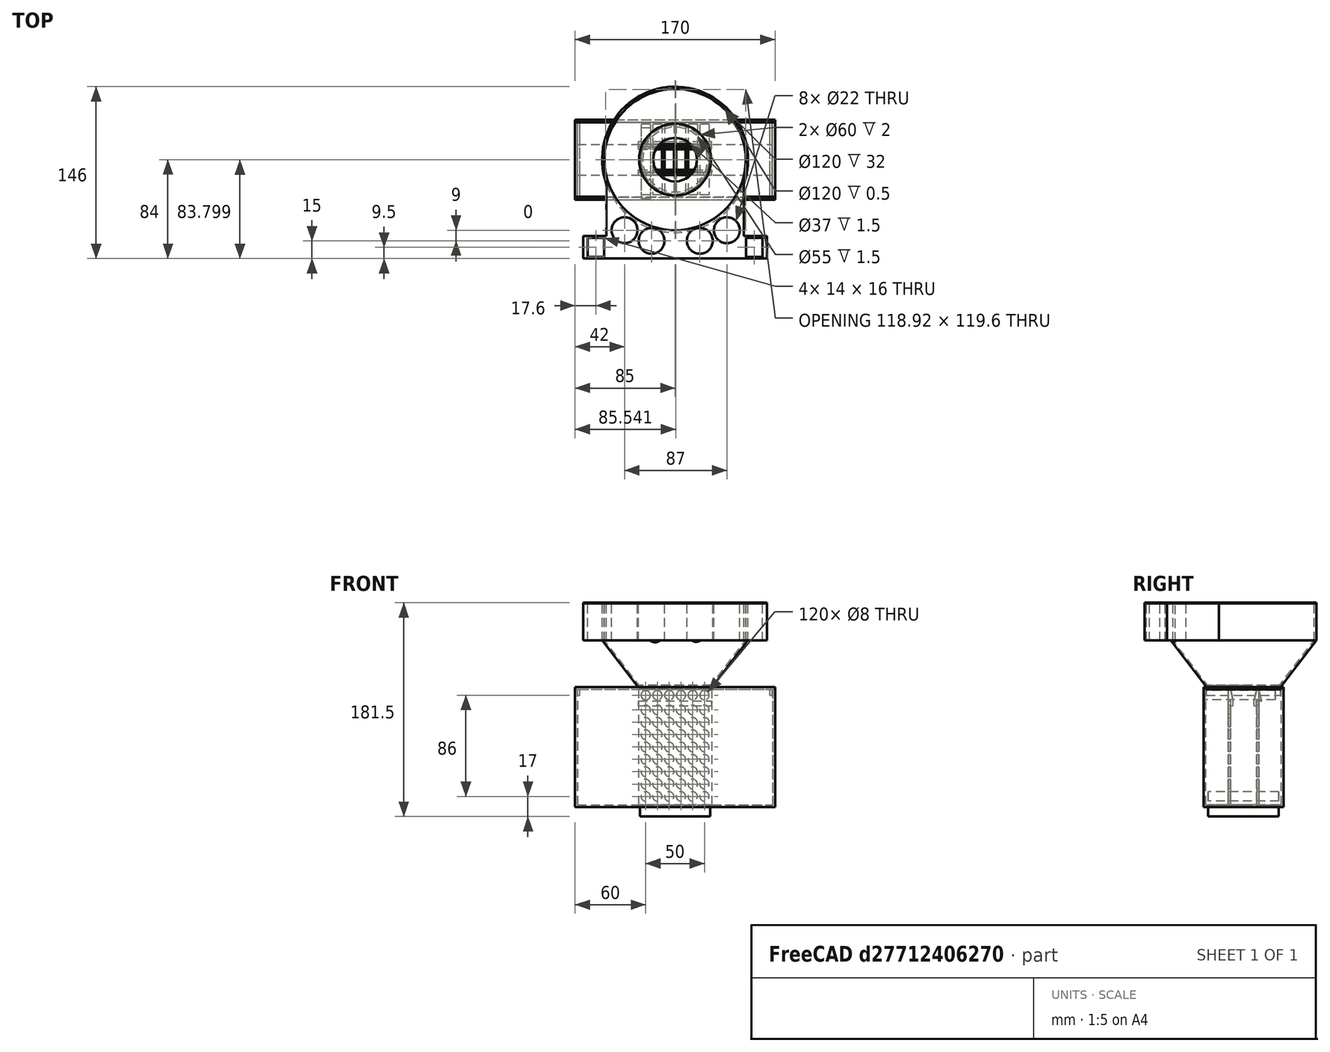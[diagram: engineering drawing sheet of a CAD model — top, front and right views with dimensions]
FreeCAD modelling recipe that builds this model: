
FCSTD DOCUMENT  (FreeCAD 0.19R24291 (Git))
Label: ventilador2
License: All rights reserved
LicenseURL: http://en.wikipedia.org/wiki/All_rights_reserved
objects: Part::Box×38, Part::Cut×37, Part::Cylinder×23, Part::MultiFuse×13, Part::FeaturePython×7, Part::Feature×7, Mesh::Feature×5, Part::Cone×4, Sketcher::SketchObject×1, PartDesign::Pad×1, PartDesign::Body×1
note: 129 computed .brp shape members not serialized (recipe doc carries the construction recipe); baked Part::Feature solids carry a one-line shape summary decoded from their .brp

FEATURE [Part::Box] Box  label="freeze1"
  AttacherType = Attacher::AttachEngine3D
  Height = 98
  Length = 166
  Width = 19
FEATURE [Part::Box] Box001  label="freeze2"
  AttacherType = Attacher::AttachEngine3D
  Height = 98
  Length = 166
  Placement = pos=(0,45,0) rot=(0,0,1;0rad)
  Width = 19
FEATURE [Part::Box] Box002  label="Cube"
  AttacherType = Attacher::AttachEngine3D
  Height = 2
  Length = 170
  Placement = pos=(-2,-2,-2) rot=(0,0,1;0rad)
  Width = 68
FEATURE [Part::Box] Box003  label="Cube001"
  AttacherType = Attacher::AttachEngine3D
  Height = 100
  Length = 170
  Placement = pos=(-2,-2,0) rot=(0,0,1;0rad)
  Width = 2
FEATURE [Part::Box] Box004  label="Cube002"
  AttacherType = Attacher::AttachEngine3D
  Height = 88
  Length = 170
  Placement = pos=(-2,19,0) rot=(0,0,1;0rad)
  Width = 2
FEATURE [Part::Box] Box005  label="Cube003"
  AttacherType = Attacher::AttachEngine3D
  Height = 88
  Length = 170
  Placement = pos=(-2,43,0) rot=(0,0,1;0rad)
  Width = 2
FEATURE [Part::Box] Box006  label="Cube004"
  AttacherType = Attacher::AttachEngine3D
  Height = 100
  Length = 170
  Placement = pos=(-2,64,0) rot=(0,0,1;0rad)
  Width = 2
FEATURE [Part::Box] Box007  label="Cube005"
  AttacherType = Attacher::AttachEngine3D
  Height = 98
  Length = 2
  Placement = pos=(-2,0,0) rot=(0,0,1;0rad)
  Width = 64
FEATURE [Part::Box] Box008  label="Cube006"
  AttacherType = Attacher::AttachEngine3D
  Height = 98
  Length = 2
  Placement = pos=(166,0,0) rot=(0,0,1;0rad)
  Width = 66
FEATURE [Part::MultiFuse] Fusion  label="base_caja"
  Shapes = -> [Box002,Box003,Box004,Box005,Box006,Box007,Box008]
FEATURE [Part::Box] Box009  label="Cube007"
  AttacherType = Attacher::AttachEngine3D
  Height = 12
  Length = 165
  Placement = pos=(0.5,19,88) rot=(0,0,1;0rad)
  Width = 2
FEATURE [Part::Box] Box010  label="Cube008"
  AttacherType = Attacher::AttachEngine3D
  Height = 12
  Length = 165
  Placement = pos=(0.5,43.2,88) rot=(0,0,1;0rad)
  Width = 2
FEATURE [Part::Box] Box011  label="Cube009"
  AttacherType = Attacher::AttachEngine3D
  Height = 2
  Length = 170
  Placement = pos=(-2,0.5,98) rot=(0,0,1;0rad)
  Width = 63
FEATURE [Part::MultiFuse] Fusion001  label="tapa_caja"
  Shapes = -> [Box009,Box010,Box011]
FEATURE [Part::Cylinder] Cylinder
  Angle = 360
  AttacherType = Attacher::AttachEngine3D
  Height = 10
  Placement = pos=(83,32,98) rot=(0,0,1;0rad)
  Radius = 30
FEATURE [Part::FeaturePython] Point  label="Center"  # WARN: FeaturePython — macro-defined, semantics opaque (R4)
  X = 83
  Y = 32
  Z = 108
FEATURE [Part::Cylinder] Cylinder001
  Angle = 360
  AttacherType = Attacher::AttachEngine3D
  Height = 10
  Placement = pos=(83,32,-10) rot=(0,0,1;0rad)
  Radius = 30
FEATURE [Part::Cylinder] Cylinder002
  Angle = 360
  AttacherType = Attacher::AttachEngine3D
  Height = 10
  Placement = pos=(83,32,-10) rot=(0,0,1;0rad)
  Radius = 30
FEATURE [Part::Cut] Cut  label="base1"
  Base = -> Fusion
  Tool = -> Cylinder001
FEATURE [Part::Cut] Cut001  label="tapa1"
  Base = -> Fusion001
  Tool = -> Cylinder
FEATURE [Part::Box] Box012  label="Cube010"
  AttacherType = Attacher::AttachEngine3D
  Height = 10
  Length = 52
  Placement = pos=(0,5,88) rot=(0,0,1;0rad)
  Width = 45
FEATURE [Part::Box] Box013  label="Cube011"
  AttacherType = Attacher::AttachEngine3D
  Height = 10
  Length = 52
  Placement = pos=(114,5,88) rot=(0,0,1;0rad)
  Width = 45
FEATURE [Part::Cut] Cut002
  Base = -> Cut001
  Tool = -> Box012
FEATURE [Part::Cut] Cut003
  Base = -> Cut002
  Tool = -> Box013
FEATURE [Part::Box] Box014  label="Cube012"
  AttacherType = Attacher::AttachEngine3D
  Height = 4
  Length = 48
  Placement = pos=(59,19,96) rot=(0,0,1;0rad)
  Width = 2
FEATURE [Part::Box] Box015  label="Cube013"
  AttacherType = Attacher::AttachEngine3D
  Height = 4
  Length = 48
  Placement = pos=(59,43.2,96) rot=(0,0,1;0rad)
  Width = 2
FEATURE [Part::Box] Box016  label="Cube014"
  AttacherType = Attacher::AttachEngine3D
  Height = 100
  Length = 52
  Placement = pos=(0,5,0) rot=(0,0,1;0rad)
  Width = 45
FEATURE [Part::Box] Box017  label="Cube015"
  AttacherType = Attacher::AttachEngine3D
  Height = 100
  Length = 52
  Placement = pos=(114,5,0) rot=(0,0,1;0rad)
  Width = 45
FEATURE [Part::Box] Box018  label="Cube016"
  AttacherType = Attacher::AttachEngine3D
  Height = 4
  Length = 48
  Placement = pos=(59,19,-2) rot=(0,0,1;0rad)
  Width = 2
FEATURE [Part::Box] Box019  label="Cube017"
  AttacherType = Attacher::AttachEngine3D
  Height = 4
  Length = 48
  Placement = pos=(59,43,-2) rot=(0,0,1;0rad)
  Width = 2
FEATURE [Part::MultiFuse] Fusion002  label="tapa2"
  Shapes = -> [Cut003,Box014,Box015]
FEATURE [Part::Cylinder] Cylinder003
  Angle = 360
  AttacherType = Attacher::AttachEngine3D
  Height = 60
  Placement = pos=(58,59,93) rot=(1,0,0;1.5708rad)
  Radius = 4
FEATURE [Part::FeaturePython] Array  # Draft array (typed FeaturePython)
  Angle = 360
  ArrayType = 0
  Axis = (0,0,1)
  Base = -> Cylinder003
  Center = (0,0,0)
  Count = 6
  ExpandArray = false
  Fuse = false
  IntervalAxis = (0,0,0)
  IntervalX = (10,0,0)
  IntervalY = (0,100,0)
  IntervalZ = (0,0,100)
  NumberCircles = 3
  NumberPolar = 5
  NumberX = 6
  NumberY = 1
  NumberZ = 1
  PlacementList = 6 placements: arithmetic series from (58,59,93) step (10,0,0) to (108,59,93)
  RadialDistance = 50
  ScaleList = (6) [(1,1,1),(1,1,1),(1,1,1),(1,1,1),(1,1,1),(1,1,1)]
  Symmetry = 1
  TangentialDistance = 25
FEATURE [Part::Cylinder] Cylinder004
  Angle = 360
  AttacherType = Attacher::AttachEngine3D
  Height = 60
  Placement = pos=(58,59,93) rot=(1,0,0;1.5708rad)
  Radius = 4
FEATURE [Part::Cut] Cut004  label="tapa333"
  Base = -> Fusion002
  Tool = -> Array
FEATURE [Part::Cut] Cut005
  Base = -> Cut
  Tool = -> Box016
FEATURE [Part::Cut] Cut006
  Base = -> Cut005
  Tool = -> Box017
FEATURE [Part::MultiFuse] Fusion003
  Shapes = -> [Cut006,Box019,Box018]
FEATURE [Part::Feature] Array001001
  Placement = pos=(0,3,-86) rot=(0,0,1;0rad)
  shape: bbox 58 x 60 x 8 mm, 18 faces, 6 solids (baked)
FEATURE [Part::FeaturePython] Array001002  # Draft array (typed FeaturePython)
  Angle = 360
  ArrayType = 0
  Axis = (0,0,1)
  Base = -> Array001001
  Center = (0,0,0)
  Count = 8
  ExpandArray = false
  Fuse = false
  IntervalAxis = (0,0,0)
  IntervalX = (100,0,0)
  IntervalY = (0,100,0)
  IntervalZ = (0,0,10.5)
  NumberCircles = 3
  NumberPolar = 5
  NumberX = 1
  NumberY = 1
  NumberZ = 8
  PlacementList = 8 placements: arithmetic series from (0,3,-86) step (0,0,10.5) to (0,3,-12.5)
  RadialDistance = 50
  ScaleList = (8) [(1,1,1),(1,1,1),(1,1,1),(1,1,1),(1,1,1),(1,1,1),(1,1,1),(1,1,1)]
  Symmetry = 1
  TangentialDistance = 25
FEATURE [Part::Cut] Cut007  label="base"
  Base = -> Fusion003
  Tool = -> Array001002
FEATURE [Part::FeaturePython] Point001  label="Center001"  # WARN: FeaturePython — macro-defined, semantics opaque (R4)
  X = 83
  Y = 32
  Z = 100
FEATURE [Part::Cylinder] Cylinder005
  Angle = 360
  AttacherType = Attacher::AttachEngine3D
  Height = 1.5
  Radius = 29.5
FEATURE [Part::Cylinder] Cylinder006
  Angle = 360
  AttacherType = Attacher::AttachEngine3D
  Height = 1.5
  Radius = 27.5
FEATURE [Part::Cylinder] Cylinder007
  Angle = 360
  AttacherType = Attacher::AttachEngine3D
  Height = 10
  Radius = 27.5
FEATURE [Part::Cut] Cut008
  Base = -> Cylinder005
  Tool = -> Cylinder006
FEATURE [Part::Cut] Cut009
  Base = -> Cut008
  Tool = -> Cylinder007
FEATURE [Part::Cylinder] Cylinder008
  Angle = 360
  AttacherType = Attacher::AttachEngine3D
  Height = 1.5
  Radius = 31
FEATURE [Part::Cylinder] Cylinder009
  Angle = 360
  AttacherType = Attacher::AttachEngine3D
  Height = 1.5
  Radius = 18.5
FEATURE [Part::Cut] Cut010
  Base = -> Cylinder008
  Placement = pos=(0,0,1.5) rot=(0,0,1;0rad)
  Tool = -> Cylinder009
FEATURE [Part::MultiFuse] Fusion004  label="union1"
  Placement = pos=(83,32,98.5) rot=(0,0,1;0rad)
  Shapes = -> [Cut009,Cut010]
FEATURE [Part::FeaturePython] Point002  label="Center002"  # WARN: FeaturePython — macro-defined, semantics opaque (R4)
  X = 0
  Y = 0
  Z = 3
FEATURE [Part::Cylinder] Cylinder010
  Angle = 360
  AttacherType = Attacher::AttachEngine3D
  Height = 32
  Radius = 60
FEATURE [Part::Cylinder] Cylinder011
  Angle = 360
  AttacherType = Attacher::AttachEngine3D
  Height = 32
  Radius = 62
FEATURE [Part::Cut] Cut011
  Base = -> Cylinder011
  Placement = pos=(0,0,40) rot=(0,0,1;0rad)
  Tool = -> Cylinder010
FEATURE [Part::Cone] Cone
  Angle = 360
  AttacherType = Attacher::AttachEngine3D
  Height = 40
  Radius1 = 31
  Radius2 = 62
FEATURE [Part::Cone] Cone001
  Angle = 360
  AttacherType = Attacher::AttachEngine3D
  Height = 40
  Radius1 = 29
  Radius2 = 60
FEATURE [Part::Cut] Cut012
  Base = -> Cone
  Tool = -> Cone001
FEATURE [Part::MultiFuse] Fusion005  label="cono22"
  Placement = pos=(83,32,99.5) rot=(1,0,0;0rad)
  Shapes = -> [Cut011,Cut012]
FEATURE [Part::Cone] Cone002
  Angle = 360
  AttacherType = Attacher::AttachEngine3D
  Height = 40
  Radius1 = 29
  Radius2 = 60
FEATURE [Part::Cone] Cone003
  Angle = 360
  AttacherType = Attacher::AttachEngine3D
  Height = 40
  Radius1 = 31
  Radius2 = 62
FEATURE [Part::Cut] Cut013
  Base = -> Cone003
  Placement = pos=(83,32,99.5) rot=(0,0,1;0rad)
  Tool = -> Cone002
FEATURE [Part::Cut] Cut014  label="union"
  Base = -> Fusion004
  Tool = -> Cut013
FEATURE [Mesh::Feature] Mesh002  label="union (Meshed)"
FEATURE [Mesh::Feature] Mesh004  label="base (Meshed)"
FEATURE [Part::Feature] Cut013001
  Placement = pos=(83,32,131.5) rot=(0,0,1;0rad)
  shape: bbox 156.4 x 143.4 x 40 mm, 201 faces (baked)
FEATURE [Part::Box] Box020  label="Cube018"
  AttacherType = Attacher::AttachEngine3D
  Height = 10
  Length = 200
  Placement = pos=(-62,-48,127) rot=(0,0,1;0rad)
  Width = 200
FEATURE [Part::Cut] Cut013002
  Base = -> Cut013001
  Placement = pos=(-1.2,15,0) rot=(0,0,1;0rad)
  Tool = -> Box020
FEATURE [Part::Box] Box021  label="Cube019"
  AttacherType = Attacher::AttachEngine3D
  Height = 32
  Length = 116.8
  Placement = pos=(24.6,-49,139.5) rot=(0,0,1;0rad)
  Width = 80
FEATURE [Part::Cylinder] Cylinder012
  Angle = 360
  AttacherType = Attacher::AttachEngine3D
  Height = 100
  Placement = pos=(83,32,83) rot=(0,0,1;0rad)
  Radius = 60
FEATURE [Part::Box] Box022  label="Cube020"
  AttacherType = Attacher::AttachEngine3D
  Height = 30
  Length = 200
  Placement = pos=(0,-65,109.5) rot=(0,0,1;0rad)
  Width = 40
FEATURE [Part::Cylinder] Cylinder015
  Angle = 360
  AttacherType = Attacher::AttachEngine3D
  Height = 50
  Placement = pos=(127,-28,123) rot=(0,0,1;0rad)
  Radius = 11
FEATURE [Part::Cylinder] Cylinder016
  Angle = 360
  AttacherType = Attacher::AttachEngine3D
  Height = 50
  Placement = pos=(40,-28,123) rot=(0,0,1;0rad)
  Radius = 11
FEATURE [Part::Box] Box023  label="Cube021"
  AttacherType = Attacher::AttachEngine3D
  Height = 200
  Length = 200
  Placement = pos=(0,-86,-29) rot=(0,0,1;0rad)
  Width = 200
FEATURE [Part::Cut] Cut013008004  label="apoyo_del_cono"
  Base = -> Box021
  Refine = true
  Tool = -> Cylinder012
FEATURE [Part::Cut] Cut013008005  label="este_tiene_los_soportes2"
  Base = -> Cut013002
  Refine = true
  Tool = -> Box022
FEATURE [Part::MultiFuse] Fusion006
  Refine = true
  Shapes = -> [Cut013008004,Fusion005]
FEATURE [Part::Cylinder] Cylinder017
  Angle = 360
  AttacherType = Attacher::AttachEngine3D
  Height = 50
  Placement = pos=(104,-37,123) rot=(0,0,1;0rad)
  Radius = 11
FEATURE [Part::Cylinder] Cylinder018
  Angle = 360
  AttacherType = Attacher::AttachEngine3D
  Height = 50
  Placement = pos=(63,-37,123) rot=(0,0,1;0rad)
  Radius = 11
FEATURE [Part::Cylinder] Cylinder019
  Angle = 360
  AttacherType = Attacher::AttachEngine3D
  Height = 50
  Placement = pos=(127,-28,123) rot=(0,0,1;0rad)
  Radius = 11
FEATURE [Part::Cylinder] Cylinder020
  Angle = 360
  AttacherType = Attacher::AttachEngine3D
  Height = 50
  Placement = pos=(40,-28,123) rot=(0,0,1;0rad)
  Radius = 11
FEATURE [Part::Cylinder] Cylinder021
  Angle = 360
  AttacherType = Attacher::AttachEngine3D
  Height = 50
  Placement = pos=(104,-37,123) rot=(0,0,1;0rad)
  Radius = 11
FEATURE [Part::Cylinder] Cylinder022
  Angle = 360
  AttacherType = Attacher::AttachEngine3D
  Height = 50
  Placement = pos=(63,-37,123) rot=(0,0,1;0rad)
  Radius = 11
FEATURE [Part::Cut] Cut013008006
  Base = -> Fusion006
  Refine = true
  Tool = -> Cylinder015
FEATURE [Part::Cut] Cut013008007
  Base = -> Cut013008006
  Refine = true
  Tool = -> Cylinder016
FEATURE [Part::Cut] Cut013008008
  Base = -> Cut013008007
  Refine = true
  Tool = -> Cylinder017
FEATURE [Part::Cut] Cut013008009  label="apoyo_del_cono_con_agujeros"
  Base = -> Cut013008008
  Refine = true
  Tool = -> Cylinder018
FEATURE [Part::Cut] Cut013008010
  Base = -> Cut013008005
  Refine = true
  Tool = -> Cylinder019
FEATURE [Part::Cut] Cut013008011
  Base = -> Cut013008010
  Refine = true
  Tool = -> Cylinder020
FEATURE [Part::Cut] Cut013008012
  Base = -> Cut013008011
  Refine = true
  Tool = -> Cylinder021
FEATURE [Part::Cut] Cut013008013  label="este_tiene_los_soportes"
  Base = -> Cut013008012
  Refine = true
  Tool = -> Cylinder022
FEATURE [Part::MultiFuse] Fusion007  label="cono"
  Refine = true
  Shapes = -> [Cut013008009,Cut013008013]
FEATURE [Part::Feature] Fusion007001  label="test_cono33"
  shape: bbox 156.4 x 144 x 72 mm, 26 faces (baked)
FEATURE [Part::Cut] Cut013008014  label="test_cono"
  Base = -> Fusion007001
  Refine = true
  Tool = -> Box023
FEATURE [Part::Box] Box024  label="Cube022"
  AttacherType = Attacher::AttachEngine3D
  Height = 0.5
  Length = 156.4
  Placement = pos=(4.8,-52,171) rot=(0,0,1;0rad)
  Width = 2
FEATURE [Part::Box] Box025  label="Cube023"
  AttacherType = Attacher::AttachEngine3D
  Height = 32
  Length = 156.4
  Placement = pos=(4.8,-52,139.5) rot=(0,0,1;0rad)
  Width = 2
FEATURE [Part::Box] Box026  label="Cube024"
  AttacherType = Attacher::AttachEngine3D
  Height = 0.5
  Length = 14
  Placement = pos=(8.6,-50.5,171) rot=(0,0,1;0rad)
  Width = 2
FEATURE [Part::Box] Box027  label="Cube025"
  AttacherType = Attacher::AttachEngine3D
  Height = 80
  Length = 14
  Placement = pos=(8.6,-50.5,116) rot=(0,0,1;0rad)
  Width = 2
FEATURE [Part::Box] Box028  label="Cube026"
  AttacherType = Attacher::AttachEngine3D
  Height = 0.5
  Length = 14
  Placement = pos=(143.4,-50.5,171) rot=(0,0,1;0rad)
  Width = 2
FEATURE [Part::Box] Box029  label="Cube027"
  AttacherType = Attacher::AttachEngine3D
  Height = 80
  Length = 14
  Placement = pos=(143.4,-50.5,111) rot=(0,0,1;0rad)
  Width = 2
FEATURE [Part::MultiFuse] Fusion007002
  Refine = true
  Shapes = -> [Cut013008014,Box024]
FEATURE [Part::Cut] Cut013008015
  Base = -> Fusion007002
  Refine = true
  Tool = -> Box028
FEATURE [Part::Cut] Cut013008016  label="test_cono_2"
  Base = -> Cut013008015
  Refine = true
  Tool = -> Box026
FEATURE [Part::MultiFuse] Fusion007003
  Refine = true
  Shapes = -> [Fusion007,Box025]
FEATURE [Part::Cut] Cut013008017
  Base = -> Fusion007003
  Refine = true
  Tool = -> Box029
FEATURE [Part::Cut] Cut013008018  label="cono2"
  Base = -> Cut013008017
  Refine = true
  Tool = -> Box027
FEATURE [Mesh::Feature] Mesh005  label="cono2 (Meshed)"
FEATURE [Mesh::Feature] Mesh006  label="test_cono_2 (Meshed)"
FEATURE [Part::Box] Box030  label="Cube028"
  AttacherType = Attacher::AttachEngine3D
  Height = 5
  Length = 2
  Placement = pos=(0,0.5,93) rot=(0,0,1;0rad)
  Width = 63
FEATURE [Part::Box] Box031  label="Cube029"
  AttacherType = Attacher::AttachEngine3D
  Height = 5
  Length = 2
  Placement = pos=(163.7,0.5,93) rot=(0,0,1;0rad)
  Width = 63
FEATURE [Part::Box] Box032  label="Cube030"
  AttacherType = Attacher::AttachEngine3D
  Height = 4
  Length = 62
  Placement = pos=(52,18.7,84) rot=(0,0,1;0rad)
  Width = 2.6
FEATURE [Part::Box] Box033  label="Cube031"
  AttacherType = Attacher::AttachEngine3D
  Height = 4
  Length = 62
  Placement = pos=(52,42.9,84) rot=(0,0,1;0rad)
  Width = 2.6
FEATURE [Part::Box] Box034  label="Cube032"
  AttacherType = Attacher::AttachEngine3D
  Height = 4
  Length = 62
  Placement = pos=(52,16.7,84) rot=(0,0,1;0rad)
  Width = 6.6
FEATURE [Part::Box] Box035  label="Cube033"
  AttacherType = Attacher::AttachEngine3D
  Height = 4
  Length = 62
  Placement = pos=(52,40.9,84) rot=(0,0,1;0rad)
  Width = 6.6
FEATURE [Sketcher::SketchObject] Sketch
  FullyConstrained = false
  MapMode = 5
  Placement = pos=(52,0,0) rot=(0.57735,-0.57735,-0.57735;2.0944rad)
  sketch-geometry (3):
    g0: LineSegment StartX=-45.2 StartY=88 StartZ=0 EndX=-47.5 EndY=88 EndZ=0
    g1: LineSegment StartX=-47.5 StartY=88 StartZ=0 EndX=-45.2 EndY=98 EndZ=0
    g2: LineSegment StartX=-45.2 StartY=98 StartZ=0 EndX=-45.2 EndY=88 EndZ=0
  constraints (5):
    c: Horizontal(g0)
    c: Coincident(g0,g1)
    c: Coincident(g1,g2)
    c: Coincident(g2,g0)
    c: DistanceX(g0,g0) = 2.3
FEATURE [PartDesign::Pad] Pad
  Direction = (1,1,1)
  Length = 62
  Length2 = 100
  Placement = pos=(52,0,0) rot=(0.57735,-0.57735,-0.57735;2.0944rad)
  Profile = -> Sketch
  Reversed = true
  Type = 0
FEATURE [PartDesign::Body] Body
  Group = -> [Sketch,Pad]
  Origin = -> Origin
  Tip = -> Pad
FEATURE [Part::Feature] Body001
  shape: bbox 62 x 2.3 x 10 mm, 5 faces (baked)
FEATURE [Part::Feature] Body002
  Placement = pos=(0,-24.2,0) rot=(0,0,1;0rad)
  shape: bbox 62 x 2.3 x 10 mm, 5 faces (baked)
FEATURE [Part::Feature] Body003
  Placement = pos=(166,64.2,0) rot=(0,0,1;3.14159rad)
  shape: bbox 62 x 2.3 x 10 mm, 5 faces (baked)
FEATURE [Part::Feature] Body004
  Placement = pos=(166,88.4,0) rot=(0,0,1;3.14159rad)
  shape: bbox 62 x 2.3 x 10 mm, 5 faces (baked)
FEATURE [Part::MultiFuse] Fusion007004
  Shapes = -> [Box035,Body001,Body004]
FEATURE [Part::Cut] Cut013008019
  Base = -> Fusion007004
  Tool = -> Box033
FEATURE [Part::MultiFuse] Fusion007005
  Shapes = -> [Body003,Body002,Box034]
FEATURE [Part::Cut] Cut013008020
  Base = -> Fusion007005
  Tool = -> Box032
FEATURE [Part::Cylinder] Cylinder023
  Angle = 360
  AttacherType = Attacher::AttachEngine3D
  Height = 60
  Placement = pos=(58,59,93) rot=(1,0,0;1.5708rad)
  Radius = 4
FEATURE [Part::FeaturePython] Array001003  # Draft array (typed FeaturePython)
  Angle = 360
  ArrayType = 0
  Axis = (0,0,1)
  Base = -> Cylinder023
  Center = (0,0,0)
  Count = 6
  ExpandArray = false
  Fuse = false
  IntervalAxis = (0,0,0)
  IntervalX = (10,0,0)
  IntervalY = (0,100,0)
  IntervalZ = (0,0,100)
  NumberCircles = 3
  NumberPolar = 5
  NumberX = 6
  NumberY = 1
  NumberZ = 1
  PlacementList = 6 placements: arithmetic series from (58,59,93) step (10,0,0) to (108,59,93)
  RadialDistance = 50
  ScaleList = (6) [(1,1,1),(1,1,1),(1,1,1),(1,1,1),(1,1,1),(1,1,1)]
  Symmetry = 1
  TangentialDistance = 25
FEATURE [Part::Cylinder] Cylinder024
  Angle = 360
  AttacherType = Attacher::AttachEngine3D
  Height = 60
  Placement = pos=(58,59,93) rot=(1,0,0;1.5708rad)
  Radius = 4
FEATURE [Part::FeaturePython] Array001004  # Draft array (typed FeaturePython)
  Angle = 360
  ArrayType = 0
  Axis = (0,0,1)
  Base = -> Cylinder024
  Center = (0,0,0)
  Count = 6
  ExpandArray = false
  Fuse = false
  IntervalAxis = (0,0,0)
  IntervalX = (10,0,0)
  IntervalY = (0,100,0)
  IntervalZ = (0,0,100)
  NumberCircles = 3
  NumberPolar = 5
  NumberX = 6
  NumberY = 1
  NumberZ = 1
  PlacementList = 6 placements: arithmetic series from (58,59,93) step (10,0,0) to (108,59,93)
  RadialDistance = 50
  ScaleList = (6) [(1,1,1),(1,1,1),(1,1,1),(1,1,1),(1,1,1),(1,1,1)]
  Symmetry = 1
  TangentialDistance = 25
FEATURE [Part::Cut] Cut013008021
  Base = -> Cut013008019
  Tool = -> Array001003
FEATURE [Part::Cut] Cut013008022
  Base = -> Cut013008020
  Tool = -> Array001004
FEATURE [Part::Box] Box036  label="Cube034"
  AttacherType = Attacher::AttachEngine3D
  Height = 20
  Length = 150
  Placement = pos=(0,5,78) rot=(0,0,1;0rad)
  Width = 14
FEATURE [Part::Box] Box037  label="Cube035"
  AttacherType = Attacher::AttachEngine3D
  Height = 20
  Length = 150
  Placement = pos=(0,45,78) rot=(0,0,1;0rad)
  Width = 14
FEATURE [Part::Cut] Cut013008023
  Base = -> Cut013008021
  Tool = -> Box037
FEATURE [Part::Cut] Cut013008024
  Base = -> Cut013008022
  Tool = -> Box036
FEATURE [Part::MultiFuse] Fusion007006  label="tapa"
  Shapes = -> [Cut004,Box031,Box030,Cut013008023,Cut013008024]
FEATURE [Mesh::Feature] Mesh  label="tapa (Meshed)"
